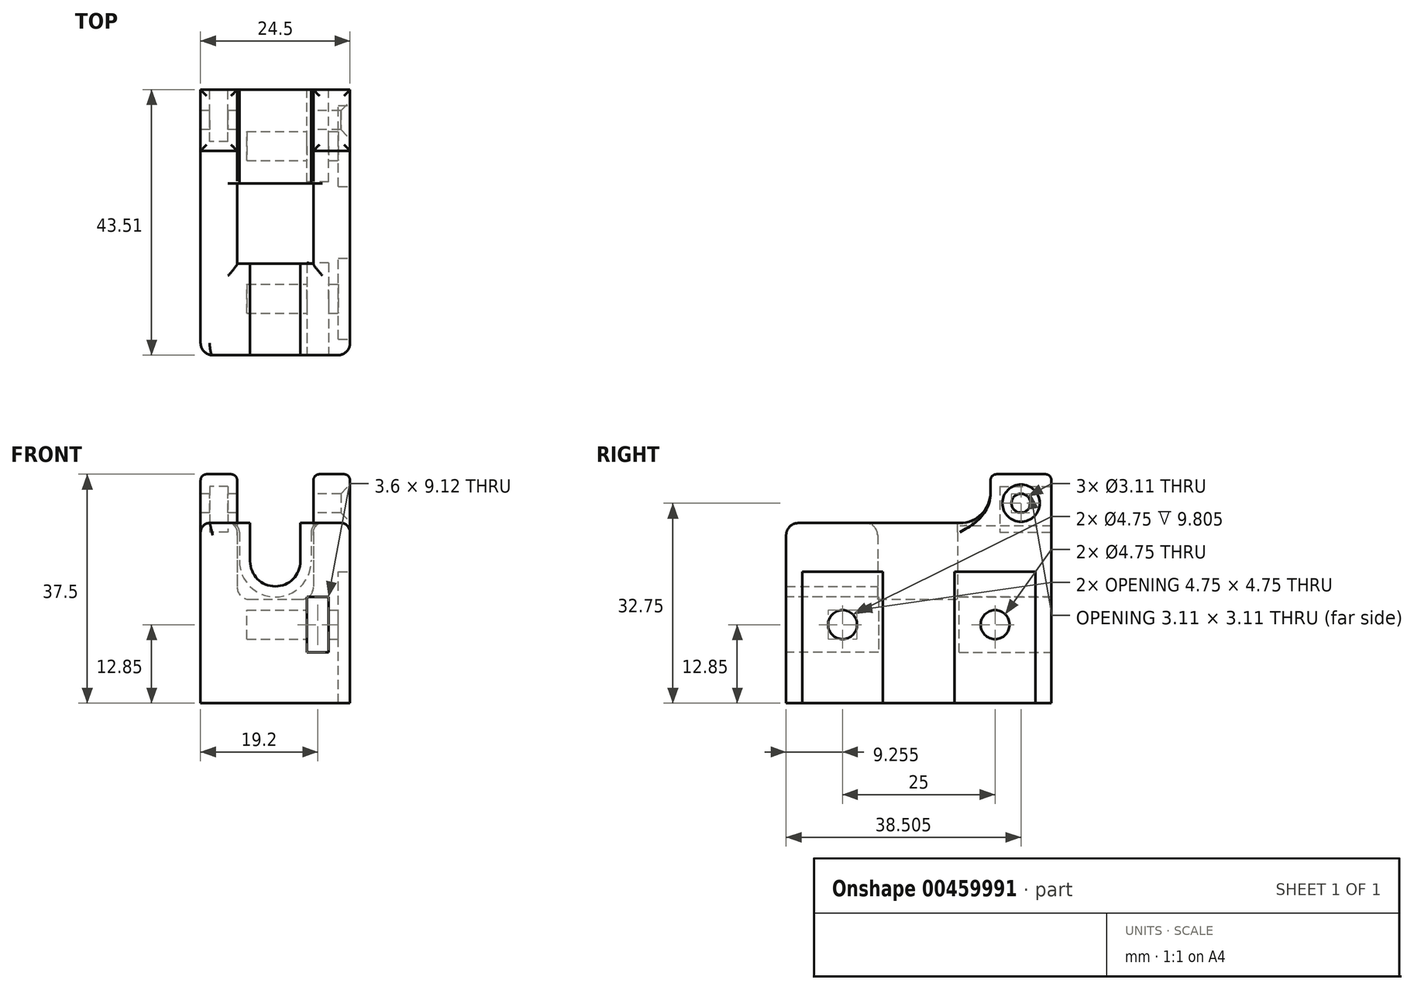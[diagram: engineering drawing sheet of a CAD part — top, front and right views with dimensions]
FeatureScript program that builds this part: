
annotation { "Feature Type Name" : "Feature", "Feature Type Description" : "" }
export const myFeature = defineFeature(function(context is Context, id is Id, definition is map)
    precondition{}
    {
        {
            var Q0;
            Q0=qCreatedBy(makeId("Front.planeOp"),FACE);
            var sketch = newSketch(context, id + "F0", { "sketchPlane" : qUnion([Q0])});
            skLineSegment(sketch, "E0.bottom", {"start": v(-6.25, 6.25) * mm, "end": v(6.25, 6.25) * mm, "construction": true});
            skLineSegment(sketch, "E0.top", {"start": v(-4.25, -6.25) * mm, "end": v(4.25, -6.25) * mm});
            skLineSegment(sketch, "E0.left", {"start": v(-6.25, 4.75) * mm, "end": v(-6.25, -4.25) * mm});
            skLineSegment(sketch, "E0.right", {"start": v(6.25, 4.75) * mm, "end": v(6.25, -4.25) * mm});
            skPoint(sketch, "E0.middle", {"position": v(0, 0) * mm});
            skLineSegment(sketch, "E1.bottom", {"start": v(-10.75, -11.25) * mm, "end": v(10.75, -11.25) * mm});
            skLineSegment(sketch, "E1.left", {"start": v(-12.25, -9.75) * mm, "end": v(-12.25, 4.75) * mm});
            skLineSegment(sketch, "E1.right", {"start": v(12.25, -9.75) * mm, "end": v(12.25, 4.75) * mm});
            skLineSegment(sketch, "E2", {"start": v(-7.75, 6.25) * mm, "end": v(-10.75, 6.25) * mm});
            skLineSegment(sketch, "E3", {"start": v(7.75, 6.25) * mm, "end": v(10.75, 6.25) * mm});
            skPoint(sketch, "E4.visualSharp", {"position": v(-6.25, -6.25) * mm});
            skArc(sketch, "E4.filletArc", {"start": v(-6.25, -4.25) * mm, "mid": v(-5.66, -5.66) * mm, "end": v(-4.25, -6.25) * mm});
            skPoint(sketch, "E5.visualSharp", {"position": v(6.25, -6.25) * mm});
            skArc(sketch, "E5.filletArc", {"start": v(4.25, -6.25) * mm, "mid": v(5.66, -5.66) * mm, "end": v(6.25, -4.25) * mm});
            skPoint(sketch, "E6.visualSharp", {"position": v(-6.25, 6.25) * mm});
            skArc(sketch, "E6.filletArc", {"start": v(-6.25, 4.75) * mm, "mid": v(-6.69, 5.81) * mm, "end": v(-7.75, 6.25) * mm});
            skPoint(sketch, "E7.visualSharp", {"position": v(6.25, 6.25) * mm});
            skArc(sketch, "E7.filletArc", {"start": v(7.75, 6.25) * mm, "mid": v(6.69, 5.81) * mm, "end": v(6.25, 4.75) * mm});
            skLineSegment(sketch, "E8", {"start": v(6.25, 0.25) * mm, "end": v(12.25, 0.25) * mm, "construction": true});
            skLineSegment(sketch, "E9", {"start": v(-6.25, 0.25) * mm, "end": v(-12.25, 0.25) * mm, "construction": true});
            skLineSegment(sketch, "E10", {"start": v(0, -6.25) * mm, "end": v(0, -11.25) * mm, "construction": true});
            skPoint(sketch, "E11.visualSharp", {"position": v(-12.25, 6.25) * mm});
            skArc(sketch, "E11.filletArc", {"start": v(-10.75, 6.25) * mm, "mid": v(-11.81, 5.81) * mm, "end": v(-12.25, 4.75) * mm});
            skPoint(sketch, "E12.visualSharp", {"position": v(-12.25, -11.25) * mm});
            skArc(sketch, "E12.filletArc", {"start": v(-12.25, -9.75) * mm, "mid": v(-11.81, -10.81) * mm, "end": v(-10.75, -11.25) * mm});
            skPoint(sketch, "E13.visualSharp", {"position": v(12.25, -11.25) * mm});
            skArc(sketch, "E13.filletArc", {"start": v(10.75, -11.25) * mm, "mid": v(11.81, -10.81) * mm, "end": v(12.25, -9.75) * mm});
            skPoint(sketch, "E14.visualSharp", {"position": v(12.25, 6.25) * mm});
            skArc(sketch, "E14.filletArc", {"start": v(12.25, 4.75) * mm, "mid": v(11.81, 5.81) * mm, "end": v(10.75, 6.25) * mm});
            skSolve(sketch);
        }
        {
            var Q0;
            Q0=makeQuery(id+"F0.imprint","IMPRINT",FACE,{"disambiguationData":[TD([[makeQuery(id+"F0.imprint","IMPRINT",EDGE,{"derivedFrom":sQuery(id+"F0.wireOp",EDGE,"E0.top")}),-1.0]])]});
            extrude(context, id + "F1", {"entities" : qUnion([Q0]), "depth" : 13.12 * mm, "offsetDistance" : 25 * mm});
        }
        {
            var Q0;
            Q0=makeQuery(id+"F1.opExtrude","CAP_FACE",FACE,{"disambiguationData":[OSD([sQuery(id+"F0.wireOp",EDGE,"E0.top"),sQuery(id+"F0.wireOp",EDGE,"E0.left"),sQuery(id+"F0.wireOp",EDGE,"E0.right"),sQuery(id+"F0.wireOp",EDGE,"E1.bottom"),sQuery(id+"F0.wireOp",EDGE,"E1.left"),sQuery(id+"F0.wireOp",EDGE,"E1.right"),sQuery(id+"F0.wireOp",EDGE,"E2"),sQuery(id+"F0.wireOp",EDGE,"E3"),sQuery(id+"F0.wireOp",EDGE,"E4.filletArc"),sQuery(id+"F0.wireOp",EDGE,"E5.filletArc"),sQuery(id+"F0.wireOp",EDGE,"E6.filletArc"),sQuery(id+"F0.wireOp",EDGE,"E7.filletArc"),sQuery(id+"F0.wireOp",EDGE,"E11.filletArc"),sQuery(id+"F0.wireOp",EDGE,"E12.filletArc"),sQuery(id+"F0.wireOp",EDGE,"E13.filletArc"),sQuery(id+"F0.wireOp",EDGE,"E14.filletArc")])],"isStart":false});
            var sketch = newSketch(context, id + "F2", { "sketchPlane" : qUnion([Q0])});
            skLineSegment(sketch, "E15.bottom", {"start": v(-10.75, -11.25) * mm, "end": v(10.75, -11.25) * mm});
            skLineSegment(sketch, "E15.top", {"start": v(-10.75, 6.25) * mm, "end": v(10.75, 6.25) * mm});
            skLineSegment(sketch, "E15.left", {"start": v(-12.25, -9.75) * mm, "end": v(-12.25, 4.75) * mm});
            skLineSegment(sketch, "E15.right", {"start": v(12.25, -9.75) * mm, "end": v(12.25, 4.75) * mm});
            skPoint(sketch, "E16.visualSharp", {"position": v(-12.25, 6.25) * mm});
            skArc(sketch, "E16.filletArc", {"start": v(-10.75, 6.25) * mm, "mid": v(-11.81, 5.81) * mm, "end": v(-12.25, 4.75) * mm});
            skPoint(sketch, "E17.visualSharp", {"position": v(-12.25, -11.25) * mm});
            skArc(sketch, "E17.filletArc", {"start": v(-12.25, -9.75) * mm, "mid": v(-11.81, -10.81) * mm, "end": v(-10.75, -11.25) * mm});
            skPoint(sketch, "E18.visualSharp", {"position": v(12.25, -11.25) * mm});
            skArc(sketch, "E18.filletArc", {"start": v(10.75, -11.25) * mm, "mid": v(11.81, -10.81) * mm, "end": v(12.25, -9.75) * mm});
            skPoint(sketch, "E19.visualSharp", {"position": v(12.25, 6.25) * mm});
            skArc(sketch, "E19.filletArc", {"start": v(12.25, 4.75) * mm, "mid": v(11.81, 5.81) * mm, "end": v(10.75, 6.25) * mm});
            skSolve(sketch);
        }
        {
            var Q0;
            Q0=qSketchRegion(id+"F2",true);
            extrude(context, id + "F3", {"entities" : qUnion([Q0]), "operationType" : NewBodyOperationType.ADD, "depth" : 15 * mm, "offsetDistance" : 25 * mm});
        }
        {
            var Q0;
            Q0=makeQuery(id+"F3.opExtrude","SWEPT_FACE",FACE,{"disambiguationData":[OSD([sQuery(id+"F2.wireOp",EDGE,"E15.top")])]});
            var sketch = newSketch(context, id + "F4", { "sketchPlane" : qUnion([Q0])});
            skLineSegment(sketch, "E20", {"start": v(-209.2, -4) * mm, "end": v(-134.75, -13.13) * mm});
            skLineSegment(sketch, "E21", {"start": v(-134.75, -13.13) * mm, "end": v(-137.84, -38.34) * mm});
            skLineSegment(sketch, "E22", {"start": v(-137.84, -38.34) * mm, "end": v(-212.28, -29.22) * mm});
            skLineSegment(sketch, "E23", {"start": v(-212.28, -29.22) * mm, "end": v(-209.2, -4) * mm});
            skLineSegment(sketch, "E24", {"start": v(-134.75, -13.13) * mm, "end": v(-209.2, -13.13) * mm, "construction": true});
            skLineSegment(sketch, "E25", {"start": v(-209.2, -4) * mm, "end": v(-209.2, -13.13) * mm, "construction": true});
            skLineSegment(sketch, "E26", {"start": v(-12.25, -13.13) * mm, "end": v(-12.25, -28.12) * mm, "construction": true});
            skLineSegment(sketch, "E27", {"start": v(12.25, -13.12) * mm, "end": v(12.25, -31.12) * mm, "construction": true});
            skSolve(sketch);
        }
        {
            var Q0;
            Q0=qSketchRegion(id+"F4",true);
            extrude(context, id + "F5", {"entities" : qUnion([Q0]), "operationType" : NewBodyOperationType.REMOVE, "oppositeDirection" : true, "depth" : 25 * mm});
        }
        {
            var Q0;
            Q0=makeQuery(id+"F1.opExtrude","CAP_FACE",FACE,{"disambiguationData":[OSD([sQuery(id+"F0.wireOp",EDGE,"E0.top"),sQuery(id+"F0.wireOp",EDGE,"E0.left"),sQuery(id+"F0.wireOp",EDGE,"E0.right"),sQuery(id+"F0.wireOp",EDGE,"E1.bottom"),sQuery(id+"F0.wireOp",EDGE,"E1.left"),sQuery(id+"F0.wireOp",EDGE,"E1.right"),sQuery(id+"F0.wireOp",EDGE,"E2"),sQuery(id+"F0.wireOp",EDGE,"E3"),sQuery(id+"F0.wireOp",EDGE,"E4.filletArc"),sQuery(id+"F0.wireOp",EDGE,"E5.filletArc"),sQuery(id+"F0.wireOp",EDGE,"E6.filletArc"),sQuery(id+"F0.wireOp",EDGE,"E7.filletArc"),sQuery(id+"F0.wireOp",EDGE,"E11.filletArc"),sQuery(id+"F0.wireOp",EDGE,"E12.filletArc"),sQuery(id+"F0.wireOp",EDGE,"E13.filletArc"),sQuery(id+"F0.wireOp",EDGE,"E14.filletArc")])],"isStart":true});
            var sketch = newSketch(context, id + "F6", { "sketchPlane" : qUnion([Q0])});
            skArc(sketch, "E28", {"start": v(-5.88, 0) * mm, "mid": v(0, -5.88) * mm, "end": v(5.88, 0) * mm});
            skPoint(sketch, "E29", {"position": v(6.69, 5.81) * mm});
            skLineSegment(sketch, "E30.top", {"start": v(-10.75, -11.25) * mm, "end": v(10.75, -11.25) * mm});
            skLineSegment(sketch, "E30.left", {"start": v(-12.25, 4.75) * mm, "end": v(-12.25, -9.75) * mm});
            skLineSegment(sketch, "E30.right", {"start": v(12.25, 4.75) * mm, "end": v(12.25, -9.75) * mm});
            skLineSegment(sketch, "E31", {"start": v(-10.75, 6.25) * mm, "end": v(-7.38, 6.25) * mm});
            skLineSegment(sketch, "E32", {"start": v(-5.87, 4.75) * mm, "end": v(-5.87, 0) * mm});
            skLineSegment(sketch, "E33", {"start": v(10.75, 6.25) * mm, "end": v(7.38, 6.25) * mm});
            skLineSegment(sketch, "E34", {"start": v(5.87, 4.75) * mm, "end": v(5.88, 0) * mm});
            skPoint(sketch, "E35.visualSharp", {"position": v(-12.25, 6.25) * mm});
            skArc(sketch, "E35.filletArc", {"start": v(-10.75, 6.25) * mm, "mid": v(-11.81, 5.81) * mm, "end": v(-12.25, 4.75) * mm});
            skPoint(sketch, "E36.visualSharp", {"position": v(-5.88, 6.25) * mm});
            skArc(sketch, "E36.filletArc", {"start": v(-5.88, 4.75) * mm, "mid": v(-6.31, 5.81) * mm, "end": v(-7.38, 6.25) * mm});
            skPoint(sketch, "E37.visualSharp", {"position": v(5.88, 6.25) * mm});
            skArc(sketch, "E37.filletArc", {"start": v(7.38, 6.25) * mm, "mid": v(6.31, 5.81) * mm, "end": v(5.88, 4.75) * mm});
            skPoint(sketch, "E38.visualSharp", {"position": v(12.25, 6.25) * mm});
            skArc(sketch, "E38.filletArc", {"start": v(12.25, 4.75) * mm, "mid": v(11.81, 5.81) * mm, "end": v(10.75, 6.25) * mm});
            skPoint(sketch, "E39.visualSharp", {"position": v(12.25, -11.25) * mm});
            skArc(sketch, "E39.filletArc", {"start": v(10.75, -11.25) * mm, "mid": v(11.81, -10.81) * mm, "end": v(12.25, -9.75) * mm});
            skPoint(sketch, "E40.visualSharp", {"position": v(-12.25, -11.25) * mm});
            skArc(sketch, "E40.filletArc", {"start": v(-12.25, -9.75) * mm, "mid": v(-11.81, -10.81) * mm, "end": v(-10.75, -11.25) * mm});
            skSolve(sketch);
        }
        {
            var Q0;
            Q0=qSketchRegion(id+"F6",true);
            extrude(context, id + "F7", {"entities" : qUnion([Q0]), "operationType" : NewBodyOperationType.ADD, "depth" : (18 - 2.62) * mm, "offsetDistance" : 25 * mm});
        }
        {
            var Q0;
            Q0=makeQuery(id+"F3.opExtrude","CAP_EDGE",EDGE,{"disambiguationData":[OSD([sQuery(id+"F2.wireOp",EDGE,"E15.top")])],"isStart":true});
            var Q1;
            Q1=makeQuery(id+"F3.opExtrude","CAP_FACE",FACE,{"disambiguationData":[OSD([sQuery(id+"F2.wireOp",EDGE,"E15.bottom"),sQuery(id+"F2.wireOp",EDGE,"E15.top"),sQuery(id+"F2.wireOp",EDGE,"E15.left"),sQuery(id+"F2.wireOp",EDGE,"E15.right"),sQuery(id+"F2.wireOp",EDGE,"E16.filletArc"),sQuery(id+"F2.wireOp",EDGE,"E17.filletArc"),sQuery(id+"F2.wireOp",EDGE,"E18.filletArc"),sQuery(id+"F2.wireOp",EDGE,"E19.filletArc")])],"isStart":false});
            fillet(context, id + "F8", {"entities" : qUnion([Q0, Q1]), "radius" : 2 * mm, "tangentPropagation" : true, "allowEdgeOverflow" : false});
        }
        {
            var Q0;
            Q0=makeQuery(id+"F7.boolean.opBoolean","MERGE",FACE,{"derivedFrom":[makeQuery(id+"F3.boolean.opBoolean","MERGE",FACE,{"derivedFrom":[makeQuery(id+"F1.opExtrude","SWEPT_FACE",FACE,{"disambiguationData":[OSD([sQuery(id+"F0.wireOp",EDGE,"E2")])]}),makeQuery(id+"F1.opExtrude","SWEPT_FACE",FACE,{"disambiguationData":[OSD([sQuery(id+"F0.wireOp",EDGE,"E3")])]}),makeQuery(id+"F3.opExtrude","SWEPT_FACE",FACE,{"disambiguationData":[OSD([sQuery(id+"F2.wireOp",EDGE,"E15.top")])]})]}),makeQuery(id+"F7.opExtrude","SWEPT_FACE",FACE,{"disambiguationData":[OSD([sQuery(id+"F6.wireOp",EDGE,"E31")])]}),makeQuery(id+"F7.opExtrude","SWEPT_FACE",FACE,{"disambiguationData":[OSD([sQuery(id+"F6.wireOp",EDGE,"E33")])]})]});
            var sketch = newSketch(context, id + "F9", { "sketchPlane" : qUnion([Q0])});
            skLineSegment(sketch, "E41.bottom", {"start": v(-12.25, 15.38) * mm, "end": v(-6.25, 15.38) * mm});
            skLineSegment(sketch, "E41.top", {"start": v(-12.25, 5.38) * mm, "end": v(-6.25, 5.38) * mm});
            skLineSegment(sketch, "E41.left", {"start": v(-12.25, 15.38) * mm, "end": v(-12.25, 5.38) * mm});
            skLineSegment(sketch, "E41.right", {"start": v(-6.25, 15.38) * mm, "end": v(-6.25, 5.38) * mm});
            skLineSegment(sketch, "E42.bottom", {"start": v(6.25, 15.38) * mm, "end": v(12.25, 15.38) * mm});
            skLineSegment(sketch, "E42.top", {"start": v(6.25, 5.38) * mm, "end": v(12.25, 5.38) * mm});
            skLineSegment(sketch, "E42.left", {"start": v(6.25, 15.38) * mm, "end": v(6.25, 5.38) * mm});
            skLineSegment(sketch, "E42.right", {"start": v(12.25, 15.38) * mm, "end": v(12.25, 5.38) * mm});
            skSolve(sketch);
        }
        {
            var Q0;
            Q0=qSketchRegion(id+"F9",true);
            extrude(context, id + "F10", {"entities" : qUnion([Q0]), "operationType" : NewBodyOperationType.ADD, "depth" : 8 * mm, "hasSecondDirection" : true, "secondDirectionBound" : SecondDirectionBoundingType.UP_TO_NEXT, "secondDirectionOppositeDirection" : true, "secondDirectionDepth" : 25 * mm, "offsetDistance" : 25 * mm});
        }
        {
            var Q0;
            Q0=makeQuery(id+"F10.boolean.opBoolean","MERGE",FACE,{"derivedFrom":[makeQuery(id+"F7.opExtrude","CAP_FACE",FACE,{"disambiguationData":[OSD([sQuery(id+"F6.wireOp",EDGE,"E28"),sQuery(id+"F6.wireOp",EDGE,"E30.top"),sQuery(id+"F6.wireOp",EDGE,"E30.left"),sQuery(id+"F6.wireOp",EDGE,"E30.right"),sQuery(id+"F6.wireOp",EDGE,"E31"),sQuery(id+"F6.wireOp",EDGE,"E32"),sQuery(id+"F6.wireOp",EDGE,"E33"),sQuery(id+"F6.wireOp",EDGE,"E34"),sQuery(id+"F6.wireOp",EDGE,"E35.filletArc"),sQuery(id+"F6.wireOp",EDGE,"E36.filletArc"),sQuery(id+"F6.wireOp",EDGE,"E37.filletArc"),sQuery(id+"F6.wireOp",EDGE,"E38.filletArc"),sQuery(id+"F6.wireOp",EDGE,"E39.filletArc"),sQuery(id+"F6.wireOp",EDGE,"E40.filletArc")])],"isStart":false}),makeQuery(id+"F10.opExtrude","SWEPT_FACE",FACE,{"disambiguationData":[OSD([sQuery(id+"F9.wireOp",EDGE,"E41.bottom")])]}),makeQuery(id+"F10.opExtrude","SWEPT_FACE",FACE,{"disambiguationData":[OSD([sQuery(id+"F9.wireOp",EDGE,"E42.bottom")])]})]});
            var sketch = newSketch(context, id + "F11", { "sketchPlane" : qUnion([Q0])});
            skLineSegment(sketch, "E43.bottom", {"start": v(7.75, 12.25) * mm, "end": v(10.75, 12.25) * mm});
            skLineSegment(sketch, "E43.top", {"start": v(7.75, 4.75) * mm, "end": v(10.75, 4.75) * mm});
            skLineSegment(sketch, "E43.left", {"start": v(7.75, 12.25) * mm, "end": v(7.75, 4.75) * mm});
            skLineSegment(sketch, "E43.right", {"start": v(10.75, 12.25) * mm, "end": v(10.75, 4.75) * mm});
            skPoint(sketch, "E44", {"position": v(9.25, 12.25) * mm});
            skPoint(sketch, "E45", {"position": v(9.25, 14.25) * mm});
            skPoint(sketch, "E46.endSnap0", {"position": v(9.25, 4.75) * mm});
            skPoint(sketch, "E47", {"position": v(10.75, 8.5) * mm});
            skCircle(sketch, "E48", {"center": v(0, 0) * mm, "radius": 5.88 * mm, "construction": true});
            skLineSegment(sketch, "E49", {"start": v(12.25, 8.5) * mm, "end": v(-12.25, 8.5) * mm, "construction": true});
            skSolve(sketch);
        }
        {
            var Q0;
            Q0=qSketchRegion(id+"F11",true);
            extrude(context, id + "F12", {"entities" : qUnion([Q0]), "operationType" : NewBodyOperationType.REMOVE, "oppositeDirection" : true, "depth" : 5 * mm + (6.35 * 1.1 * 0.5) * mm});
        }
        {
            var Q0;
            Q0=makeQuery(id+"F10.boolean.opBoolean","MERGE",FACE,{"derivedFrom":[makeQuery(id+"F7.boolean.opBoolean","MERGE",FACE,{"derivedFrom":[makeQuery(id+"F3.boolean.opBoolean","MERGE",FACE,{"derivedFrom":[makeQuery(id+"F1.opExtrude","SWEPT_FACE",FACE,{"disambiguationData":[OSD([sQuery(id+"F0.wireOp",EDGE,"E1.left")])]}),makeQuery(id+"F3.opExtrude","SWEPT_FACE",FACE,{"disambiguationData":[OSD([sQuery(id+"F2.wireOp",EDGE,"E15.left")])]})]}),makeQuery(id+"F7.opExtrude","SWEPT_FACE",FACE,{"disambiguationData":[OSD([sQuery(id+"F6.wireOp",EDGE,"E30.right")])]})]}),makeQuery(id+"F10.opExtrude","SWEPT_FACE",FACE,{"disambiguationData":[OSD([sQuery(id+"F9.wireOp",EDGE,"E41.left")])]})]});
            var sketch = newSketch(context, id + "F13", { "sketchPlane" : qUnion([Q0])});
            skLineSegment(sketch, "E50", {"start": v(-10.38, 14.25) * mm, "end": v(-10.38, 4.75) * mm, "construction": true});
            skPoint(sketch, "E51", {"position": v(-10.38, 9.5) * mm});
            skCircle(sketch, "E52", {"center": v(-10.38, 9.5) * mm, "radius": 1.55 * mm});
            skLineSegment(sketch, "E53", {"start": v(-15.38, 4.75) * mm, "end": v(-5.38, 4.75) * mm, "construction": true});
            skLineSegment(sketch, "E54", {"start": v(-5.38, 4.75) * mm, "end": v(-5.38, 4.75) * mm});
            skSolve(sketch);
        }
        {
            var Q0;
            Q0=qSketchRegion(id+"F13",true);
            extrude(context, id + "F14", {"entities" : qUnion([Q0]), "operationType" : NewBodyOperationType.REMOVE, "endBound" : BoundingType.THROUGH_ALL, "oppositeDirection" : true, "depth" : 25 * mm});
        }
        {
            var Q0;
            Q0=makeQuery(id+"F10.boolean.opBoolean","MERGE",FACE,{"derivedFrom":[makeQuery(id+"F7.boolean.opBoolean","MERGE",FACE,{"derivedFrom":[makeQuery(id+"F3.boolean.opBoolean","MERGE",FACE,{"derivedFrom":[makeQuery(id+"F1.opExtrude","SWEPT_FACE",FACE,{"disambiguationData":[OSD([sQuery(id+"F0.wireOp",EDGE,"E1.right")])]}),makeQuery(id+"F3.opExtrude","SWEPT_FACE",FACE,{"disambiguationData":[OSD([sQuery(id+"F2.wireOp",EDGE,"E15.right")])]})]}),makeQuery(id+"F7.opExtrude","SWEPT_FACE",FACE,{"disambiguationData":[OSD([sQuery(id+"F6.wireOp",EDGE,"E30.left")])]})]}),makeQuery(id+"F10.opExtrude","SWEPT_FACE",FACE,{"disambiguationData":[OSD([sQuery(id+"F9.wireOp",EDGE,"E42.right")])]})]});
            var sketch = newSketch(context, id + "F15", { "sketchPlane" : qUnion([Q0])});
            skCircle(sketch, "E55", {"center": v(10.38, 9.5) * mm, "radius": 2.53 * mm});
            skSolve(sketch);
        }
        {
            var Q0;
            Q0=makeQuery(id+"F10.boolean.opBoolean","MERGE",FACE,{"derivedFrom":[makeQuery(id+"F7.opExtrude","CAP_FACE",FACE,{"disambiguationData":[OSD([sQuery(id+"F6.wireOp",EDGE,"E28"),sQuery(id+"F6.wireOp",EDGE,"E30.top"),sQuery(id+"F6.wireOp",EDGE,"E30.left"),sQuery(id+"F6.wireOp",EDGE,"E30.right"),sQuery(id+"F6.wireOp",EDGE,"E31"),sQuery(id+"F6.wireOp",EDGE,"E32"),sQuery(id+"F6.wireOp",EDGE,"E33"),sQuery(id+"F6.wireOp",EDGE,"E34"),sQuery(id+"F6.wireOp",EDGE,"E35.filletArc"),sQuery(id+"F6.wireOp",EDGE,"E36.filletArc"),sQuery(id+"F6.wireOp",EDGE,"E37.filletArc"),sQuery(id+"F6.wireOp",EDGE,"E38.filletArc"),sQuery(id+"F6.wireOp",EDGE,"E39.filletArc"),sQuery(id+"F6.wireOp",EDGE,"E40.filletArc")])],"isStart":false}),makeQuery(id+"F10.opExtrude","SWEPT_FACE",FACE,{"disambiguationData":[OSD([sQuery(id+"F9.wireOp",EDGE,"E41.bottom")])]}),makeQuery(id+"F10.opExtrude","SWEPT_FACE",FACE,{"disambiguationData":[OSD([sQuery(id+"F9.wireOp",EDGE,"E42.bottom")])]})]});
            var sketch = newSketch(context, id + "F16", { "sketchPlane" : qUnion([Q0])});
            skLineSegment(sketch, "E56", {"start": v(10.75, 8.5) * mm, "end": v(-12.25, 8.5) * mm, "construction": true});
            skPoint(sketch, "E57", {"position": v(7.75, 8.5) * mm});
            skSolve(sketch);
        }
        {
            var Q0;
            Q0=makeQuery(id+"F14.boolean.opBoolean","INTERSECT",EDGE,{"derivedFrom":[makeQuery(id+"F10.boolean.opBoolean","MERGE",FACE,{"derivedFrom":[makeQuery(id+"F7.boolean.opBoolean","MERGE",FACE,{"derivedFrom":[makeQuery(id+"F3.boolean.opBoolean","MERGE",FACE,{"derivedFrom":[makeQuery(id+"F1.opExtrude","SWEPT_FACE",FACE,{"disambiguationData":[OSD([sQuery(id+"F0.wireOp",EDGE,"E1.right")])]}),makeQuery(id+"F3.opExtrude","SWEPT_FACE",FACE,{"disambiguationData":[OSD([sQuery(id+"F2.wireOp",EDGE,"E15.right")])]})]}),makeQuery(id+"F7.opExtrude","SWEPT_FACE",FACE,{"disambiguationData":[OSD([sQuery(id+"F6.wireOp",EDGE,"E30.left")])]})]}),makeQuery(id+"F10.opExtrude","SWEPT_FACE",FACE,{"disambiguationData":[OSD([sQuery(id+"F9.wireOp",EDGE,"E42.right")])]})]}),makeQuery(id+"F14.opExtrude","SWEPT_FACE",FACE,{"disambiguationData":[OSD([sQuery(id+"F13.wireOp",EDGE,"E52")])]})]});
            chamfer(context, id + "F17", {"entities" : qUnion([Q0]), "width" : 1.5 * mm, "tangentPropagation" : true});
        }
        {
            var Q0;
            Q0=makeQuery(id+"F10.opExtrude","CAP_FACE",FACE,{"disambiguationData":[OSD([sQuery(id+"F9.wireOp",EDGE,"E42.bottom"),sQuery(id+"F9.wireOp",EDGE,"E42.top"),sQuery(id+"F9.wireOp",EDGE,"E42.left"),sQuery(id+"F9.wireOp",EDGE,"E42.right")])],"isStart":false});
            var Q1;
            Q1=makeQuery(id+"F10.opExtrude","CAP_FACE",FACE,{"disambiguationData":[OSD([sQuery(id+"F9.wireOp",EDGE,"E41.bottom"),sQuery(id+"F9.wireOp",EDGE,"E41.top"),sQuery(id+"F9.wireOp",EDGE,"E41.left"),sQuery(id+"F9.wireOp",EDGE,"E41.right")])],"isStart":false});
            fillet(context, id + "F18", {"entities" : qUnion([Q0, Q1]), "radius" : 1 * mm, "tangentPropagation" : true, "allowEdgeOverflow" : false});
        }
        {
            var Q0;
            Q0=makeQuery(id+"F7.boolean.opBoolean","MERGE",FACE,{"derivedFrom":[makeQuery(id+"F3.boolean.opBoolean","MERGE",FACE,{"derivedFrom":[makeQuery(id+"F1.opExtrude","SWEPT_FACE",FACE,{"disambiguationData":[OSD([sQuery(id+"F0.wireOp",EDGE,"E1.bottom")])]}),makeQuery(id+"F3.opExtrude","SWEPT_FACE",FACE,{"disambiguationData":[OSD([sQuery(id+"F2.wireOp",EDGE,"E15.bottom")])]})]}),makeQuery(id+"F7.opExtrude","SWEPT_FACE",FACE,{"disambiguationData":[OSD([sQuery(id+"F6.wireOp",EDGE,"E30.top")])]})]});
            var sketch = newSketch(context, id + "F19", { "sketchPlane" : qUnion([Q0])});
            skLineSegment(sketch, "E58.bottom", {"start": v(12.25, -15.37) * mm, "end": v(-12.25, -15.37) * mm});
            skLineSegment(sketch, "E58.top", {"start": v(12.25, 28.12) * mm, "end": v(-12.25, 28.12) * mm});
            skLineSegment(sketch, "E58.left", {"start": v(12.25, -15.38) * mm, "end": v(12.25, 28.12) * mm});
            skLineSegment(sketch, "E58.right", {"start": v(-12.25, -15.38) * mm, "end": v(-12.25, 28.12) * mm});
            skSolve(sketch);
        }
        {
            var Q0;
            Q0=qSketchRegion(id+"F19",true);
            var Q1;
            Q1=makeQuery(id+"F7.boolean.opBoolean","MERGE",FACE,{"derivedFrom":[makeQuery(id+"F3.boolean.opBoolean","MERGE",FACE,{"derivedFrom":[makeQuery(id+"F1.opExtrude","SWEPT_FACE",FACE,{"disambiguationData":[OSD([sQuery(id+"F0.wireOp",EDGE,"E13.filletArc")])]}),makeQuery(id+"F3.opExtrude","SWEPT_FACE",FACE,{"disambiguationData":[OSD([sQuery(id+"F2.wireOp",EDGE,"E18.filletArc")])]})]}),makeQuery(id+"F7.opExtrude","SWEPT_FACE",FACE,{"disambiguationData":[OSD([sQuery(id+"F6.wireOp",EDGE,"E40.filletArc")])]})]});
            var Q2;
            Q2=makeQuery(id+"F1.opExtrude","SWEPT_BODY",BODY,{"disambiguationData":[OSD([sQuery(id+"F0.wireOp",EDGE,"E0.top"),sQuery(id+"F0.wireOp",EDGE,"E0.left"),sQuery(id+"F0.wireOp",EDGE,"E0.right"),sQuery(id+"F0.wireOp",EDGE,"E1.bottom"),sQuery(id+"F0.wireOp",EDGE,"E1.left"),sQuery(id+"F0.wireOp",EDGE,"E1.right"),sQuery(id+"F0.wireOp",EDGE,"E2"),sQuery(id+"F0.wireOp",EDGE,"E3"),sQuery(id+"F0.wireOp",EDGE,"E4.filletArc"),sQuery(id+"F0.wireOp",EDGE,"E5.filletArc"),sQuery(id+"F0.wireOp",EDGE,"E6.filletArc"),sQuery(id+"F0.wireOp",EDGE,"E7.filletArc"),sQuery(id+"F0.wireOp",EDGE,"E11.filletArc"),sQuery(id+"F0.wireOp",EDGE,"E12.filletArc"),sQuery(id+"F0.wireOp",EDGE,"E13.filletArc"),sQuery(id+"F0.wireOp",EDGE,"E14.filletArc")])]});
            extrude(context, id + "F20", {"entities" : qUnion([Q0]), "operationType" : NewBodyOperationType.ADD, "depth" : 12 * mm, "offsetDistance" : 25 * mm, "hasSecondDirection" : true, "secondDirectionOppositeDirection" : true, "secondDirectionDepth" : 2 * mm, "secondDirectionBoundEntityFace" : qUnion([Q1]), "secondDirectionBoundEntityBody" : qUnion([Q2])});
        }
        {
            var Q0;
            Q0=makeQuery(id+"F20.opExtrude","SWEPT_EDGE",EDGE,{"disambiguationData":[OSD([sQuery(id+"F19.wireOp",EDGE,"E58.top"),sQuery(id+"F19.wireOp",EDGE,"E58.left")])]});
            var Q1;
            Q1=makeQuery(id+"F20.opExtrude","SWEPT_EDGE",EDGE,{"disambiguationData":[OSD([sQuery(id+"F19.wireOp",EDGE,"E58.top"),sQuery(id+"F19.wireOp",EDGE,"E58.right")])]});
            fillet(context, id + "F21", {"entities" : qUnion([Q0, Q1]), "radius" : 2 * mm, "allowEdgeOverflow" : false});
        }
        {
            var Q0;
            Q0=makeQuery(id+"F15.imprint","IMPRINT",FACE,{"disambiguationData":[TD([[makeQuery(id+"F15.imprint","IMPRINT",EDGE,{"derivedFrom":sQuery(id+"F15.wireOp",EDGE,"E55")}),-1.0]])]});
            var sketch = newSketch(context, id + "F22", { "sketchPlane" : qUnion([Q0])});
            skLineSegment(sketch, "E59.bottom", {"start": v(-25.5, -23.25) * mm, "end": v(-12.25, -23.25) * mm});
            skLineSegment(sketch, "E59.top", {"start": v(-25.5, -1.75) * mm, "end": v(-12.25, -1.75) * mm});
            skLineSegment(sketch, "E59.left", {"start": v(-25.5, -23.25) * mm, "end": v(-25.5, -1.75) * mm});
            skLineSegment(sketch, "E59.right", {"start": v(-12.25, -23.25) * mm, "end": v(-12.25, -1.75) * mm});
            skLineSegment(sketch, "E60.bottom", {"start": v(-0.5, -23.25) * mm, "end": v(12.75, -23.25) * mm});
            skLineSegment(sketch, "E60.top", {"start": v(-0.5, -1.75) * mm, "end": v(12.75, -1.75) * mm});
            skLineSegment(sketch, "E60.left", {"start": v(-0.5, -23.25) * mm, "end": v(-0.5, -1.75) * mm});
            skLineSegment(sketch, "E60.right", {"start": v(12.75, -23.25) * mm, "end": v(12.75, -1.75) * mm});
            skPoint(sketch, "E61", {"position": v(-18.88, -1.75) * mm});
            skPoint(sketch, "E62", {"position": v(6.13, -1.75) * mm});
            skLineSegment(sketch, "E63", {"start": v(-18.88, -12.5) * mm, "end": v(6.13, -12.5) * mm, "construction": true});
            skPoint(sketch, "E63.startSnap0", {"position": v(-12.25, -12.5) * mm});
            skLineSegment(sketch, "E64", {"start": v(-28.12, 2.52) * mm, "end": v(15.37, 2.52) * mm, "construction": true});
            skPoint(sketch, "E65", {"position": v(-6.37, 2.52) * mm});
            skPoint(sketch, "E66", {"position": v(-6.37, -12.5) * mm});
            skSolve(sketch);
        }
        {
            var Q0;
            Q0=qSketchRegion(id+"F22",true);
            extrude(context, id + "F23", {"entities" : qUnion([Q0]), "operationType" : NewBodyOperationType.REMOVE, "oppositeDirection" : true, "depth" : 1.9 * mm, "offsetDistance" : 25 * mm});
        }
        {
            var Q0;
            Q0=makeQuery(id+"F23.boolean.opBoolean","COPY",FACE,{"derivedFrom":makeQuery(id+"F23.opExtrude","CAP_FACE",FACE,{"disambiguationData":[OSD([sQuery(id+"F22.wireOp",EDGE,"E59.bottom"),sQuery(id+"F22.wireOp",EDGE,"E59.top"),sQuery(id+"F22.wireOp",EDGE,"E59.left"),sQuery(id+"F22.wireOp",EDGE,"E59.right")])],"isStart":false})});
            var sketch = newSketch(context, id + "F24", { "sketchPlane" : qUnion([Q0])});
            skLineSegment(sketch, "E67", {"start": v(-18.87, -1.75) * mm, "end": v(-18.88, -23.25) * mm, "construction": true});
            skLineSegment(sketch, "E68", {"start": v(6.12, -1.75) * mm, "end": v(6.13, -23.25) * mm, "construction": true});
            skCircle(sketch, "E69", {"center": v(-18.87, -10.4) * mm, "radius": 2.38 * mm});
            skCircle(sketch, "E70", {"center": v(6.13, -10.4) * mm, "radius": 2.38 * mm});
            skSolve(sketch);
        }
        {
            var Q0;
            Q0=makeQuery(id+"F16.imprint","IMPRINT",FACE,{"disambiguationData":[TD([[makeQuery(id+"F16.imprint","IMPRINT",EDGE,{"derivedFrom":makeQuery(id+"F7.opExtrude","CAP_EDGE",EDGE,{"disambiguationData":[OSD([sQuery(id+"F6.wireOp",EDGE,"E28")])],"isStart":false})}),-1.0]])]});
            var sketch = newSketch(context, id + "F25", { "sketchPlane" : qUnion([Q0])});
            skLineSegment(sketch, "E71.bottom", {"start": v(-8.75, -14.96) * mm, "end": v(-5.15, -14.96) * mm});
            skLineSegment(sketch, "E71.top", {"start": v(-8.75, -5.84) * mm, "end": v(-5.15, -5.84) * mm});
            skLineSegment(sketch, "E71.left", {"start": v(-8.75, -14.96) * mm, "end": v(-8.75, -5.84) * mm});
            skLineSegment(sketch, "E71.right", {"start": v(-5.15, -14.96) * mm, "end": v(-5.15, -5.84) * mm});
            skPoint(sketch, "E72", {"position": v(-5.15, -10.4) * mm});
            skSolve(sketch);
        }
        {
            var Q0;
            Q0=makeQuery(id+"F20.boolean.opBoolean","MERGE",FACE,{"derivedFrom":[makeQuery(id+"F3.opExtrude","CAP_FACE",FACE,{"disambiguationData":[OSD([sQuery(id+"F2.wireOp",EDGE,"E15.bottom"),sQuery(id+"F2.wireOp",EDGE,"E15.top"),sQuery(id+"F2.wireOp",EDGE,"E15.left"),sQuery(id+"F2.wireOp",EDGE,"E15.right"),sQuery(id+"F2.wireOp",EDGE,"E16.filletArc"),sQuery(id+"F2.wireOp",EDGE,"E17.filletArc"),sQuery(id+"F2.wireOp",EDGE,"E18.filletArc"),sQuery(id+"F2.wireOp",EDGE,"E19.filletArc")])],"isStart":false}),makeQuery(id+"F20.opExtrude","SWEPT_FACE",FACE,{"disambiguationData":[OSD([sQuery(id+"F19.wireOp",EDGE,"E58.top")])]})]});
            var sketch = newSketch(context, id + "F26", { "sketchPlane" : qUnion([Q0])});
            skLineSegment(sketch, "E73.bottom", {"start": v(8.75, -5.84) * mm, "end": v(5.15, -5.84) * mm});
            skLineSegment(sketch, "E73.top", {"start": v(8.75, -14.96) * mm, "end": v(5.15, -14.96) * mm});
            skLineSegment(sketch, "E73.left", {"start": v(8.75, -5.84) * mm, "end": v(8.75, -14.96) * mm});
            skLineSegment(sketch, "E73.right", {"start": v(5.15, -5.84) * mm, "end": v(5.15, -14.96) * mm});
            skSolve(sketch);
        }
        {
            var Q0;
            Q0=qSketchRegion(id+"F25",true);
            extrude(context, id + "F27", {"entities" : qUnion([Q0]), "operationType" : NewBodyOperationType.REMOVE, "oppositeDirection" : true, "depth" : 15.12 * mm, "offsetDistance" : 25 * mm});
        }
        {
            var Q0;
            Q0=qSketchRegion(id+"F26",true);
            extrude(context, id + "F28", {"entities" : qUnion([Q0]), "operationType" : NewBodyOperationType.REMOVE, "oppositeDirection" : true, "depth" : 15.12 * mm, "offsetDistance" : 25 * mm});
        }
        {
            var Q0;
            Q0=makeQuery(id+"F24.imprint","IMPRINT",FACE,{"disambiguationData":[TD([[makeQuery(id+"F24.imprint","IMPRINT",EDGE,{"derivedFrom":sQuery(id+"F24.wireOp",EDGE,"E69")}),1.0]])]});
            var Q1;
            Q1=makeQuery(id+"F24.imprint","IMPRINT",FACE,{"disambiguationData":[TD([[makeQuery(id+"F24.imprint","IMPRINT",EDGE,{"derivedFrom":sQuery(id+"F24.wireOp",EDGE,"E70")}),1.0]])]});
            var Q2;
            Q2=sQuery(id+"F24.wireOp",EDGE,"E69");
            extrude(context, id + "F29", {"entities" : qUnion([Q0, Q1]), "operationType" : NewBodyOperationType.REMOVE, "surfaceEntities" : qUnion([Q2]), "oppositeDirection" : true, "depth" : 15 * mm, "offsetDistance" : 25 * mm});
        }
        {
            var Q0;
            Q0=makeQuery(id+"F3.opExtrude","CAP_FACE",FACE,{"disambiguationData":[OSD([sQuery(id+"F2.wireOp",EDGE,"E15.bottom"),sQuery(id+"F2.wireOp",EDGE,"E15.top"),sQuery(id+"F2.wireOp",EDGE,"E15.left"),sQuery(id+"F2.wireOp",EDGE,"E15.right"),sQuery(id+"F2.wireOp",EDGE,"E16.filletArc"),sQuery(id+"F2.wireOp",EDGE,"E17.filletArc"),sQuery(id+"F2.wireOp",EDGE,"E18.filletArc"),sQuery(id+"F2.wireOp",EDGE,"E19.filletArc")])],"isStart":true});
            var sketch = newSketch(context, id + "F30", { "sketchPlane" : qUnion([Q0])});
            skCircle(sketch, "E74", {"center": v(0, 0) * mm, "radius": 4.12 * mm});
            skLineSegment(sketch, "E75", {"start": v(-4.12, 0) * mm, "end": v(-4.13, 8) * mm});
            skLineSegment(sketch, "E76", {"start": v(-4.13, 8) * mm, "end": v(4.12, 8) * mm});
            skLineSegment(sketch, "E77", {"start": v(4.12, 8) * mm, "end": v(4.12, 0) * mm});
            skSolve(sketch);
        }
        {
            var Q0;
            Q0 = qSketchRegion(id + "F30", true);
            extrude(context, id + "F31", {"entities" : qUnion([Q0]), "operationType" : NewBodyOperationType.REMOVE, "oppositeDirection" : true, "depth" : 25 * mm, "offsetDistance" : 25 * mm});
        }
        {
            var Q0;
            Q0=makeQuery(id+"F10.boolean.opBoolean","INTERSECT",EDGE,{"derivedFrom":[makeQuery(id+"F7.boolean.opBoolean","MERGE",FACE,{"derivedFrom":[makeQuery(id+"F3.boolean.opBoolean","MERGE",FACE,{"derivedFrom":[makeQuery(id+"F1.opExtrude","SWEPT_FACE",FACE,{"disambiguationData":[OSD([sQuery(id+"F0.wireOp",EDGE,"E2")])]}),makeQuery(id+"F1.opExtrude","SWEPT_FACE",FACE,{"disambiguationData":[OSD([sQuery(id+"F0.wireOp",EDGE,"E3")])]}),makeQuery(id+"F3.opExtrude","SWEPT_FACE",FACE,{"disambiguationData":[OSD([sQuery(id+"F2.wireOp",EDGE,"E15.top")])]})]}),makeQuery(id+"F7.opExtrude","SWEPT_FACE",FACE,{"disambiguationData":[OSD([sQuery(id+"F6.wireOp",EDGE,"E31")])]}),makeQuery(id+"F7.opExtrude","SWEPT_FACE",FACE,{"disambiguationData":[OSD([sQuery(id+"F6.wireOp",EDGE,"E33")])]})]}),makeQuery(id+"F10.opExtrude","SWEPT_FACE",FACE,{"disambiguationData":[OSD([sQuery(id+"F9.wireOp",EDGE,"E42.top")])]})]});
            var Q1;
            Q1=makeQuery(id+"F10.boolean.opBoolean","INTERSECT",EDGE,{"derivedFrom":[makeQuery(id+"F7.boolean.opBoolean","MERGE",FACE,{"derivedFrom":[makeQuery(id+"F3.boolean.opBoolean","MERGE",FACE,{"derivedFrom":[makeQuery(id+"F1.opExtrude","SWEPT_FACE",FACE,{"disambiguationData":[OSD([sQuery(id+"F0.wireOp",EDGE,"E2")])]}),makeQuery(id+"F1.opExtrude","SWEPT_FACE",FACE,{"disambiguationData":[OSD([sQuery(id+"F0.wireOp",EDGE,"E3")])]}),makeQuery(id+"F3.opExtrude","SWEPT_FACE",FACE,{"disambiguationData":[OSD([sQuery(id+"F2.wireOp",EDGE,"E15.top")])]})]}),makeQuery(id+"F7.opExtrude","SWEPT_FACE",FACE,{"disambiguationData":[OSD([sQuery(id+"F6.wireOp",EDGE,"E31")])]}),makeQuery(id+"F7.opExtrude","SWEPT_FACE",FACE,{"disambiguationData":[OSD([sQuery(id+"F6.wireOp",EDGE,"E33")])]})]}),makeQuery(id+"F10.opExtrude","SWEPT_FACE",FACE,{"disambiguationData":[OSD([sQuery(id+"F9.wireOp",EDGE,"E41.top")])]})]});
            fillet(context, id + "F32", {"entities" : qUnion([Q0, Q1]), "radius" : 5 * mm, "tangentPropagation" : true, "allowEdgeOverflow" : false});
        }
    });
